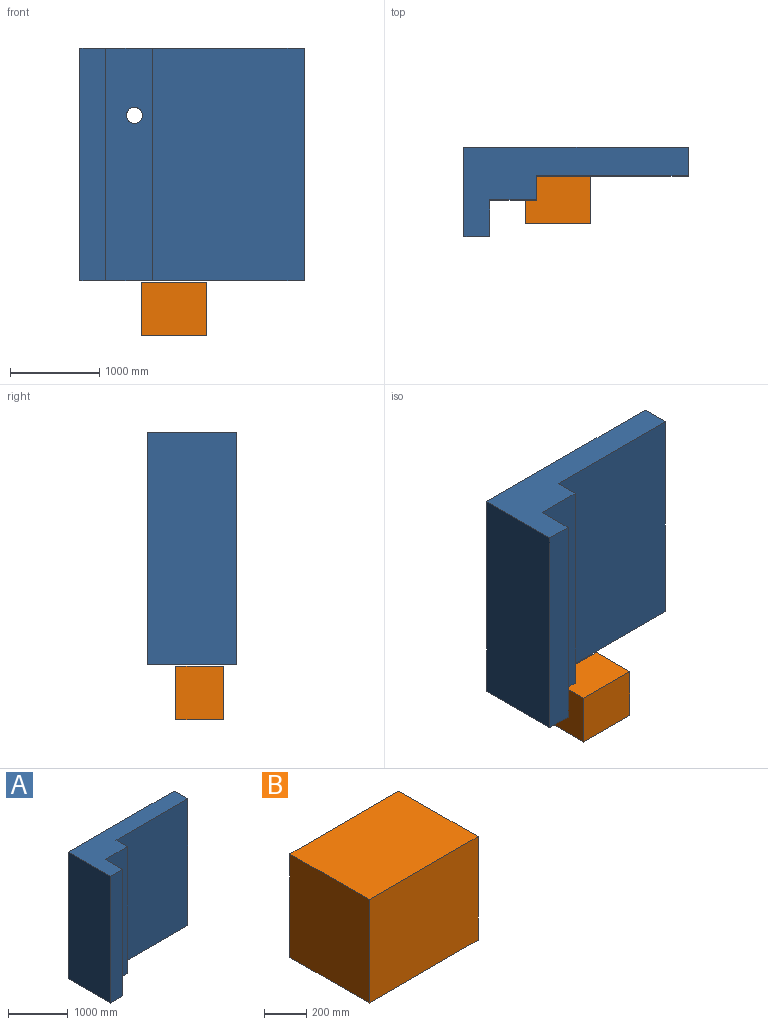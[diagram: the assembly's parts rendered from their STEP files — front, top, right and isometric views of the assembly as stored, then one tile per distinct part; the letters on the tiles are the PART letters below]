
ASSEMBLY  parts=2 mates=1
PART A: 11 faces, bbox 2510x1000x2600 mm
  f0: plane 2600x1000mm, normal (-1,0,0), area 2600000mm2, adj f1,f7,f8,f9
  f1: plane 2600x290mm, normal (0,-1,0), area 754000mm2, adj f0,f2,f8,f9
  f2: plane 2600x410mm, normal (1,0,0), area 1066000mm2, adj f1,f3,f8,f9
  f3: plane 2600x520mm, normal (0,-1,0), area 1326553.1mm2, adj f2,f4,f8,f9,f10
  f4: plane 2600x270mm, normal (1,0,0), area 702000mm2, adj f3,f5,f8,f9
  f5: plane 2600x1700mm, normal (0,-1,0), area 4420000mm2, adj f4,f6,f8,f9
  f6: plane 2600x320mm, normal (1,0,0), area 832000mm2, adj f5,f7,f8,f9
  f7: plane 2600x2510mm, normal (0,1,0), area 6500553.1mm2, adj f0,f6,f8,f9,f10
  f8: plane 2510x1000mm, normal (0,0,1), area 1140800mm2, adj f0,f1,f2,f3,f4,f5,f6,f7
  f9: plane 2510x1000mm, normal (0,0,-1), area 1140800mm2, adj f0,f1,f2,f3,f4,f5,f6,f7
  f10: cylinder r=90mm len=590mm, axis (0,-1,0), area 333637.1mm2, adj f3,f7
PART B: 6 faces, bbox 730x530x600 mm
  f0: plane 730x600mm, normal (0,-1,0), area 438000mm2, adj f1,f3,f4,f5
  f1: plane 600x530mm, normal (1,0,0), area 318000mm2, adj f0,f2,f4,f5
  f2: plane 730x600mm, normal (0,1,0), area 438000mm2, adj f1,f3,f4,f5
  f3: plane 600x530mm, normal (-1,0,0), area 318000mm2, adj f0,f2,f4,f5
  f4: plane 730x530mm, normal (0,0,1), area 386900mm2, adj f0,f1,f2,f3
  f5: plane 730x530mm, normal (0,0,-1), area 386900mm2, adj f0,f1,f2,f3
PLACE A t=(-3919.03,6791.23,-5814.28)mm
PLACE B rot(axis=(0,0,1),0deg) t=(-2867.03,7206.23,-6430.28)mm
MATE planar A.f5 <-> B.f2  axis (0,-1,0) through (-2259.03,7471.23,-4514.28)mm
